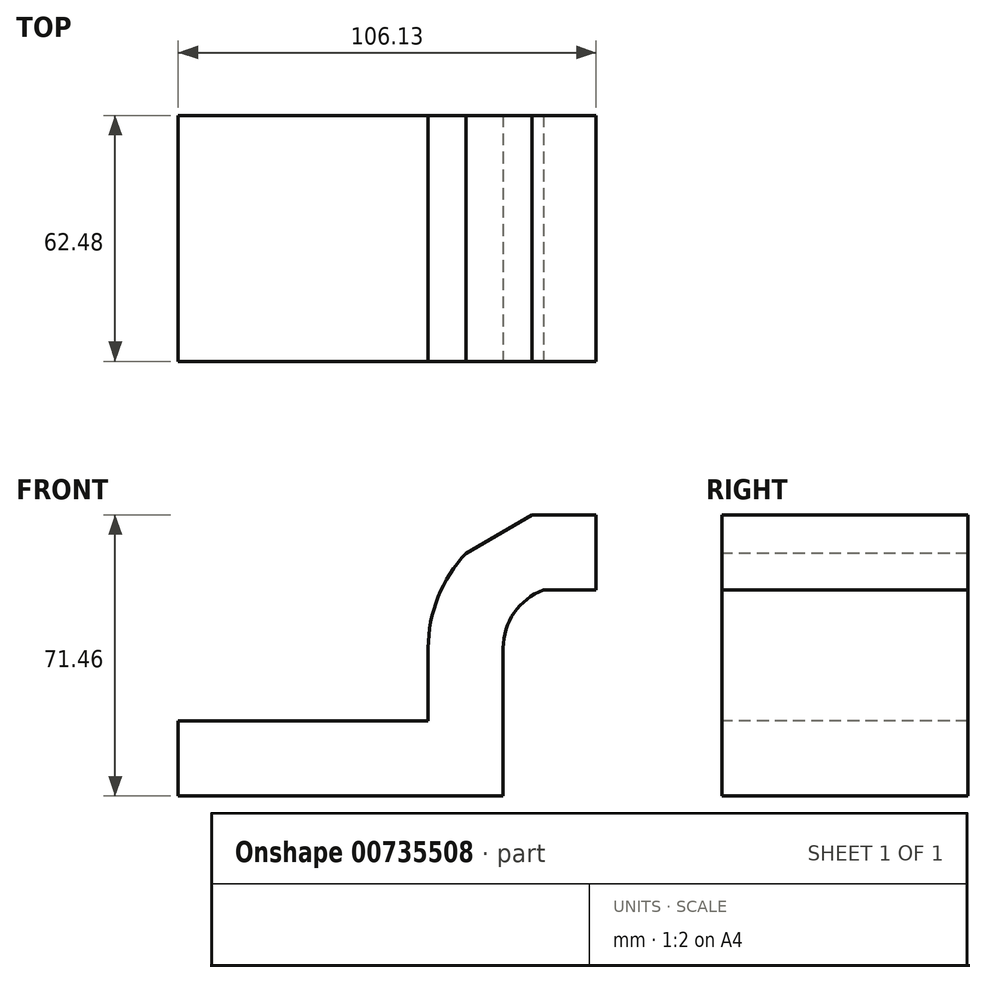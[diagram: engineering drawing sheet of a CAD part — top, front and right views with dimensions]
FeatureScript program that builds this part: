
annotation { "Feature Type Name" : "Feature", "Feature Type Description" : "" }
export const myFeature = defineFeature(function(context is Context, id is Id, definition is map)
    precondition{}
    {
        {
            var Q0;
            Q0=qCreatedBy(makeId("Front.planeOp"),FACE);
            var sketch = newSketch(context, id + "F0", { "sketchPlane" : qUnion([Q0])});
            skLineSegment(sketch, "E0.bottom", {"start": v(41.28, -9.52) * mm, "end": v(-41.27, -9.53) * mm});
            skLineSegment(sketch, "E0.top", {"start": v(41.27, 9.53) * mm, "end": v(-41.28, 9.53) * mm});
            skLineSegment(sketch, "E0.left", {"start": v(41.28, -9.52) * mm, "end": v(41.28, 9.53) * mm});
            skLineSegment(sketch, "E0.right", {"start": v(-41.27, -9.52) * mm, "end": v(-41.28, 9.53) * mm});
            skPoint(sketch, "E0.middle", {"position": v(0, 0) * mm});
            skLineSegment(sketch, "E1.bottom", {"start": v(115.66, 34.93) * mm, "end": v(64.86, 34.93) * mm});
            skLineSegment(sketch, "E1.top", {"start": v(115.66, 66.68) * mm, "end": v(64.86, 66.68) * mm});
            skLineSegment(sketch, "E1.left", {"start": v(115.66, 34.93) * mm, "end": v(115.66, 66.68) * mm});
            skLineSegment(sketch, "E1.right", {"start": v(64.86, 34.93) * mm, "end": v(64.86, 66.68) * mm});
            skPoint(sketch, "E1.middle", {"position": v(90.26, 50.8) * mm});
            skLineSegment(sketch, "E2", {"start": v(70.9, 42.88) * mm, "end": v(85.73, 42.88) * mm});
            skLineSegment(sketch, "E3", {"start": v(41.27, 9.53) * mm, "end": v(41.27, 28.05) * mm});
            skArc(sketch, "E4", {"start": v(41.28, 28.05) * mm, "mid": v(44.07, 37.05) * mm, "end": v(51.47, 42.88) * mm});
            skLineSegment(sketch, "E5", {"start": v(70.9, 42.88) * mm, "end": v(51.47, 42.88) * mm});
            skLineSegment(sketch, "E6.0", {"start": v(70.9, 61.93) * mm, "end": v(85.73, 61.93) * mm});
            skLineSegment(sketch, "E6.1", {"start": v(70.9, 61.93) * mm, "end": v(48.65, 61.93) * mm});
            skArc(sketch, "E6.2", {"start": v(22.23, 28.05) * mm, "mid": v(29.61, 49.53) * mm, "end": v(48.65, 61.93) * mm});
            skLineSegment(sketch, "E6.3", {"start": v(22.23, 9.53) * mm, "end": v(22.23, 28.05) * mm});
            skLineSegment(sketch, "E7", {"start": v(85.73, 66.68) * mm, "end": v(85.73, 34.93) * mm});
            skFitSpline(sketch, "E8", {"points": [v(-41.28, 9.53) * mm, v(48.65, 61.93) * mm], "startDerivative": vector(89.92, 52.4) * mm, "endDerivative": vector(89.92, 52.4) * mm});
            skSolve(sketch);
        }
        {
            var Q0;
            Q0=makeQuery(id+"F0.imprint","IMPRINT",FACE,{"disambiguationData":[TD([[makeQuery(id+"F0.imprint","IMPRINT",EDGE,{"derivedFrom":sQuery(id+"F0.wireOp",EDGE,"E0.bottom")}),-1.0]])]});
            var Q1;
            {var subQ1=sQuery(id+"F0.wireOp",EDGE,"E3");Q1=makeQuery(id+"F0.imprint","IMPRINT",FACE,{"disambiguationData":[TD([[makeQuery(id+"F0.imprint","IMPRINT",EDGE,{"derivedFrom":subQ1}),1.0]])]});}
            extrude(context, id + "F1", {"entities" : qUnion([Q0, Q1]), "endBound" : BoundingType.SYMMETRIC, "oppositeDirection" : true, "depth" : 62.48 * mm, "offsetDistance" : 25.4 * mm});
        }
    });
